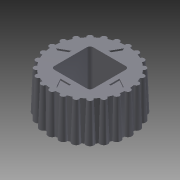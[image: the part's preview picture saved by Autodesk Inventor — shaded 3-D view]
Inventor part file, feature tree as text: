
AUTODESK INVENTOR PART (.ipt)
format: ipt  version: 2013 (Build 170138000, 138)  size: 289,280 bytes
history: native  units: in
note: dims shown in document units (in); Inventor stores cm internally (conversion verified against a paired STEP export)
features: extrude x4, sketch x4, reference x1, other x1
ambient origin geometry x8: Origin, YZ Plane, XZ Plane, XY Plane, X Axis, Y Axis, Z Axis, Center Point
bodies: Solid1 (feature_tree)
feature tree (10):
  extrude  "Extrusion1"  Depth=0.005in TaperAngle=0.0deg
  extrude  "Extrusion3"  Depth=1.0in TaperAngle=0.0deg
  extrude  "Extrusion4"  TaperAngle=0.0deg  [1 undecoded]
  sketch  "Sketch1"  dims[d0=0.125in d1=0.0137in d4=0.005in d5=0.0in]
  reference  "Reference1"
  sketch  "Sketch3"  dims[d6=0.005in d7=0.0in d8=1.0in d9=0.0in]
  sketch  "Sketch4"  dims[d10=0.0in d11=0.0in]
  sketch  "Sketch5"
  other  "Srf1"
  extrude  "ExtrusionSrf1"  [1 undecoded]
note: 2 required parameter values undecoded (feature->parameter linkage not recoverable at this tier; creation-order binding heuristic only, values carry confidence <= 0.55)
